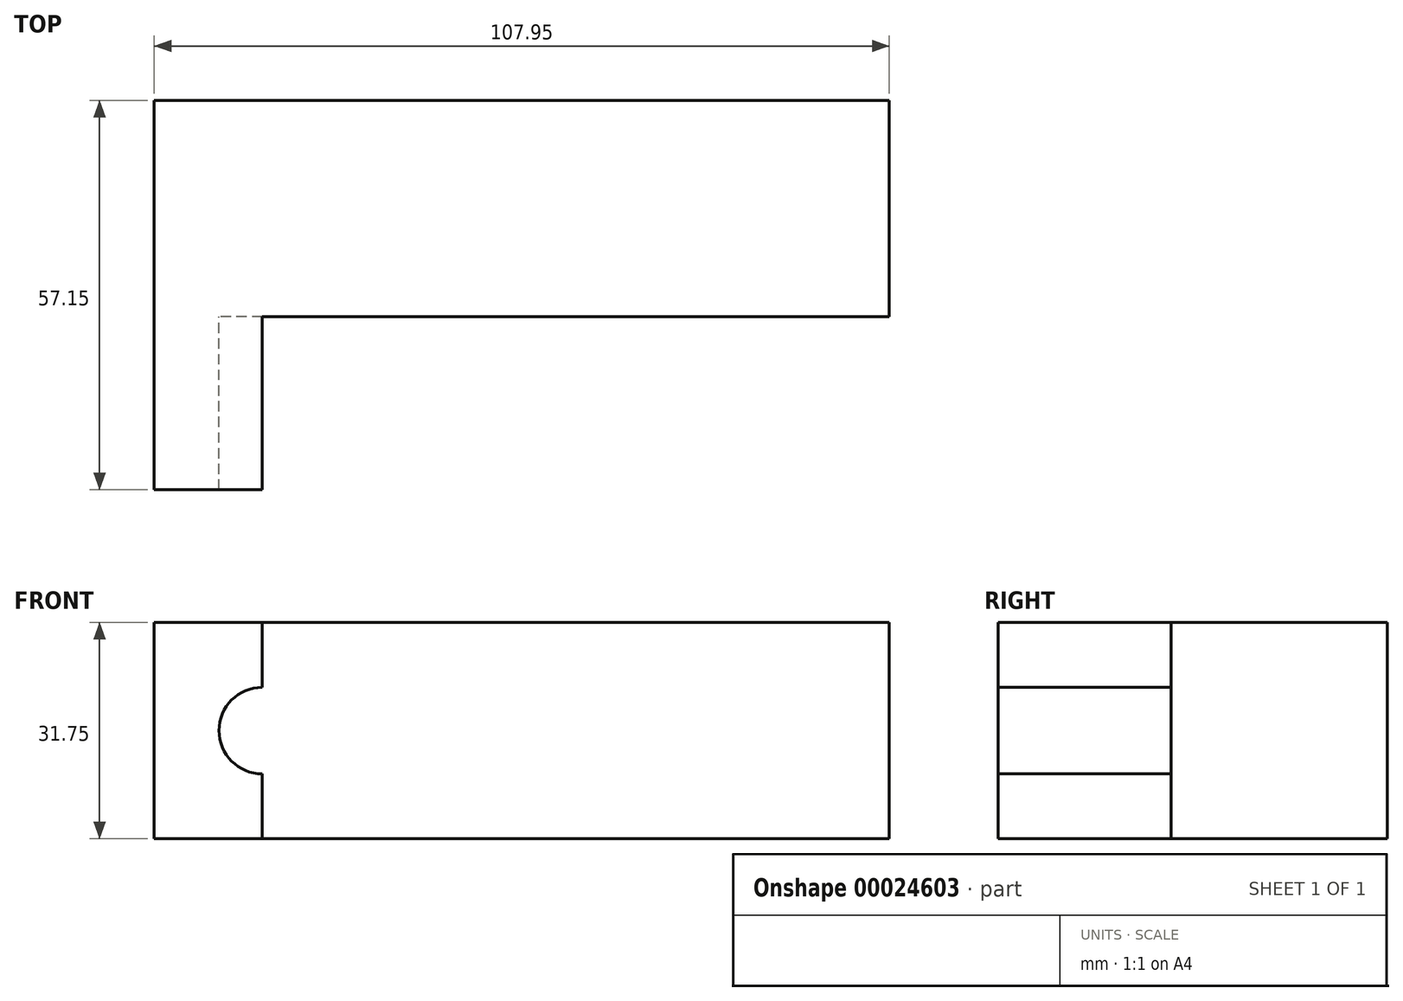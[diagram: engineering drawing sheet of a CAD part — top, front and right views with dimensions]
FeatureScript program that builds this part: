
annotation { "Feature Type Name" : "Feature", "Feature Type Description" : "" }
export const myFeature = defineFeature(function(context is Context, id is Id, definition is map)
    precondition{}
    {
        {
            var Q0;
            Q0=qCreatedBy(makeId("Front.planeOp"),FACE);
            var sketch = newSketch(context, id + "F0", { "sketchPlane" : qUnion([Q0])});
            skLineSegment(sketch, "E0.bottom", {"start": v(-26.18, -7.4) * mm, "end": v(81.77, -7.4) * mm});
            skLineSegment(sketch, "E0.top", {"start": v(-26.18, -39.16) * mm, "end": v(81.77, -39.16) * mm});
            skLineSegment(sketch, "E0.left", {"start": v(-26.18, -7.4) * mm, "end": v(-26.18, -39.16) * mm});
            skLineSegment(sketch, "E0.right", {"start": v(81.77, -7.4) * mm, "end": v(81.77, -39.16) * mm});
            skSolve(sketch);
        }
        {
            var Q0;
            Q0 = qSketchRegion(id + "F0", true);
            extrude(context, id + "F1", {"entities" : qUnion([Q0]), "depth" : 31.75 * mm});
        }
        {
            var Q0;
            Q0=makeQuery(id+"F1.opExtrude","CAP_FACE",FACE,{"disambiguationData":[OSD([sQuery(id+"F0.wireOp",EDGE,"E0.bottom"),sQuery(id+"F0.wireOp",EDGE,"E0.top"),sQuery(id+"F0.wireOp",EDGE,"E0.left"),sQuery(id+"F0.wireOp",EDGE,"E0.right")])],"isStart":false});
            var sketch = newSketch(context, id + "F2", { "sketchPlane" : qUnion([Q0])});
            skLineSegment(sketch, "E1.0", {"start": v(-10.3, -7.4) * mm, "end": v(-10.3, -39.16) * mm});
            skCircle(sketch, "E2", {"center": v(-10.3, -23.28) * mm, "radius": 6.35 * mm});
            skCircle(sketch, "E3", {"center": v(-10.3, -23.28) * mm, "radius": 15.88 * mm});
            skSolve(sketch);
        }
        {
            var Q0;
            {var subQ0=makeQuery(id+"F1.opExtrude","CAP_EDGE",EDGE,{"disambiguationData":[OSD([sQuery(id+"F0.wireOp",EDGE,"E0.left")])],"isStart":false});var subQ3=makeQuery(id+"F1.opExtrude","CAP_EDGE",EDGE,{"disambiguationData":[OSD([sQuery(id+"F0.wireOp",EDGE,"E0.bottom")])],"isStart":false});var subQ4=makeQuery(id+"F2.imprint","INTERSECT",VERTEX,{"derivedFrom":[subQ3,subQ0]});Q0=makeQuery(id+"F2.imprint","IMPRINT",FACE,{"disambiguationData":[TD([[makeQuery(id+"F2.imprint","IMPRINT",EDGE,{"disambiguationData":[TD([[subQ4,-1.0]])],"derivedFrom":subQ0}),1.0]])]});}
            var Q1;
            {var subQ0=makeQuery(id+"F1.opExtrude","CAP_EDGE",EDGE,{"disambiguationData":[OSD([sQuery(id+"F0.wireOp",EDGE,"E0.left")])],"isStart":false});var subQ3=makeQuery(id+"F1.opExtrude","CAP_EDGE",EDGE,{"disambiguationData":[OSD([sQuery(id+"F0.wireOp",EDGE,"E0.top")])],"isStart":false});var subQ4=makeQuery(id+"F2.imprint","INTERSECT",VERTEX,{"derivedFrom":[subQ3,subQ0]});Q1=makeQuery(id+"F2.imprint","IMPRINT",FACE,{"disambiguationData":[TD([[makeQuery(id+"F2.imprint","IMPRINT",EDGE,{"disambiguationData":[TD([[subQ4,1.0]])],"derivedFrom":subQ0}),1.0]])]});}
            var Q2;
            {var subQ2=sQuery(id+"F2.wireOp",EDGE,"E1.0");var subQ5=sQuery(id+"F2.wireOp",EDGE,"E2");var subQ7=makeQuery(id+"F2.imprint","INTERSECT",VERTEX,{"disambiguationData":[OD(0.0)],"derivedFrom":[subQ2,subQ5]});Q2=makeQuery(id+"F2.imprint","IMPRINT",FACE,{"disambiguationData":[TD([[makeQuery(id+"F2.imprint","IMPRINT",EDGE,{"disambiguationData":[TD([[subQ7,-1.0]])],"derivedFrom":subQ5}),-1.0]])]});}
            extrude(context, id + "F3", {"entities" : qUnion([Q0, Q1, Q2]), "operationType" : NewBodyOperationType.ADD, "depth" : 25.4 * mm});
        }
    });
